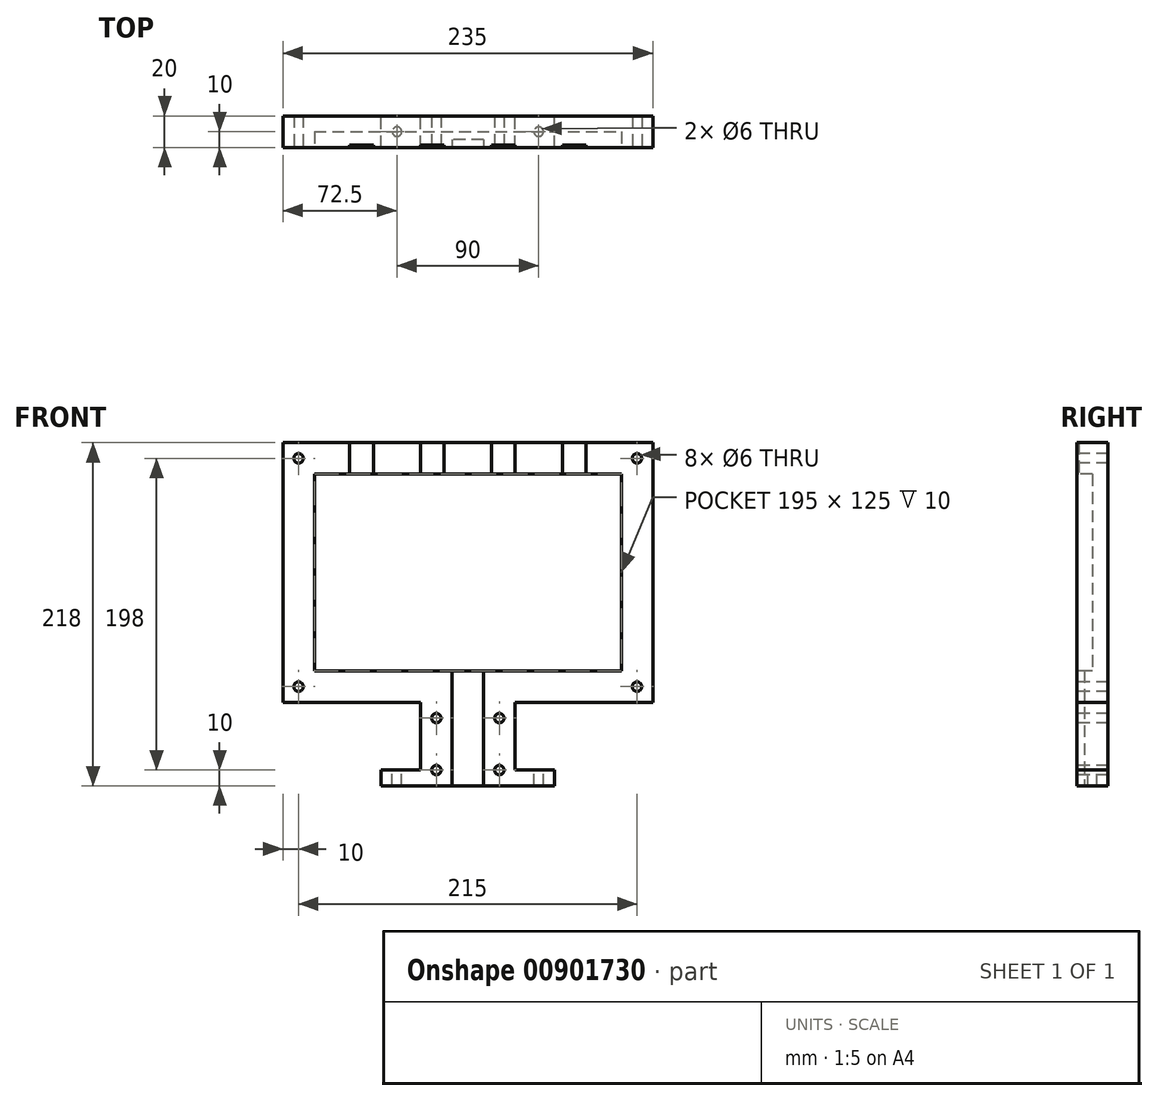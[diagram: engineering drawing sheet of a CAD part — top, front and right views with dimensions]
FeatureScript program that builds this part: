
annotation { "Feature Type Name" : "Feature", "Feature Type Description" : "" }
export const myFeature = defineFeature(function(context is Context, id is Id, definition is map)
    precondition{}
    {
        {
            var Q0;
            Q0=qCreatedBy(makeId("Front.planeOp"),FACE);
            var sketch = newSketch(context, id + "F0", { "sketchPlane" : qUnion([Q0])});
            skLineSegment(sketch, "E0", {"start": v(0, 0) * mm, "end": v(0, 10) * mm});
            skLineSegment(sketch, "E1", {"start": v(0, 10) * mm, "end": v(25, 10) * mm});
            skLineSegment(sketch, "E2", {"start": v(25, 10) * mm, "end": v(25, 53) * mm});
            skLineSegment(sketch, "E3", {"start": v(25, 53) * mm, "end": v(-62.5, 53) * mm});
            skLineSegment(sketch, "E4", {"start": v(-62.5, 53) * mm, "end": v(-62.5, 218) * mm});
            skLineSegment(sketch, "E5", {"start": v(-62.5, 218) * mm, "end": v(172.5, 218) * mm});
            skLineSegment(sketch, "E6", {"start": v(172.5, 218) * mm, "end": v(172.5, 53) * mm});
            skLineSegment(sketch, "E7", {"start": v(172.5, 53) * mm, "end": v(85, 53) * mm});
            skLineSegment(sketch, "E8", {"start": v(85, 53) * mm, "end": v(85, 10) * mm});
            skLineSegment(sketch, "E9", {"start": v(85, 10) * mm, "end": v(110, 10) * mm});
            skLineSegment(sketch, "E10", {"start": v(110, 10) * mm, "end": v(110, 0) * mm});
            skLineSegment(sketch, "E11", {"start": v(110, 0) * mm, "end": v(0, 0) * mm});
            skSolve(sketch);
        }
        {
            var Q0;
            Q0=makeQuery(id+"F0.imprint","IMPRINT",FACE,{"disambiguationData":[TD([[makeQuery(id+"F0.imprint","IMPRINT",EDGE,{"derivedFrom":sQuery(id+"F0.wireOp",EDGE,"E0")}),-1.0]])]});
            extrude(context, id + "F1", {"entities" : qUnion([Q0]), "depth" : 20 * mm, "offsetDistance" : 25 * mm});
        }
        {
            var Q0;
            Q0=makeQuery(id+"F1.opExtrude","CAP_FACE",FACE,{"disambiguationData":[OSD([sQuery(id+"F0.wireOp",EDGE,"E0"),sQuery(id+"F0.wireOp",EDGE,"E1"),sQuery(id+"F0.wireOp",EDGE,"E2"),sQuery(id+"F0.wireOp",EDGE,"E3"),sQuery(id+"F0.wireOp",EDGE,"E4"),sQuery(id+"F0.wireOp",EDGE,"E5"),sQuery(id+"F0.wireOp",EDGE,"E6"),sQuery(id+"F0.wireOp",EDGE,"E7"),sQuery(id+"F0.wireOp",EDGE,"E8"),sQuery(id+"F0.wireOp",EDGE,"E9"),sQuery(id+"F0.wireOp",EDGE,"E10"),sQuery(id+"F0.wireOp",EDGE,"E11")])],"isStart":false});
            var sketch = newSketch(context, id + "F2", { "sketchPlane" : qUnion([Q0])});
            skSolve(sketch);
        }
        {
            var Q0;
            Q0=makeQuery(id+"F2.imprint","IMPRINT",FACE,{"disambiguationData":[TD([[makeQuery(id+"F2.imprint","IMPRINT",EDGE,{"derivedFrom":makeQuery(id+"F1.opExtrude","CAP_EDGE",EDGE,{"disambiguationData":[OSD([sQuery(id+"F0.wireOp",EDGE,"E0")])],"isStart":false})}),-1.0]])]});
            var sketch = newSketch(context, id + "F3", { "sketchPlane" : qUnion([Q0])});
            skLineSegment(sketch, "E12.bottom", {"start": v(-42.5, 198) * mm, "end": v(152.5, 198) * mm});
            skLineSegment(sketch, "E12.top", {"start": v(-42.5, 73) * mm, "end": v(152.5, 73) * mm});
            skLineSegment(sketch, "E12.left", {"start": v(-42.5, 198) * mm, "end": v(-42.5, 73) * mm});
            skLineSegment(sketch, "E12.right", {"start": v(152.5, 198) * mm, "end": v(152.5, 73) * mm});
            skSolve(sketch);
        }
        {
            var Q0;
            Q0 = qSketchRegion(id + "F3", true);
            extrude(context, id + "F4", {"entities" : qUnion([Q0]), "operationType" : NewBodyOperationType.REMOVE, "oppositeDirection" : true, "depth" : 10 * mm, "offsetDistance" : 25 * mm});
        }
        {
            var Q0;
            Q0=makeQuery(id+"F2.imprint","IMPRINT",FACE,{"disambiguationData":[TD([[makeQuery(id+"F2.imprint","IMPRINT",EDGE,{"derivedFrom":makeQuery(id+"F1.opExtrude","CAP_EDGE",EDGE,{"disambiguationData":[OSD([sQuery(id+"F0.wireOp",EDGE,"E0")])],"isStart":false})}),-1.0]])]});
            var sketch = newSketch(context, id + "F5", { "sketchPlane" : qUnion([Q0])});
            skLineSegment(sketch, "E13.bottom", {"start": v(45, 73) * mm, "end": v(65, 73) * mm});
            skLineSegment(sketch, "E13.top", {"start": v(45, 0) * mm, "end": v(65, 0) * mm});
            skLineSegment(sketch, "E13.left", {"start": v(45, 73) * mm, "end": v(45, 0) * mm});
            skLineSegment(sketch, "E13.right", {"start": v(65, 73) * mm, "end": v(65, 0) * mm});
            skSolve(sketch);
        }
        {
            var Q0;
            Q0 = qSketchRegion(id + "F5", true);
            extrude(context, id + "F6", {"entities" : qUnion([Q0]), "operationType" : NewBodyOperationType.REMOVE, "oppositeDirection" : true, "depth" : 5 * mm, "offsetDistance" : 25 * mm});
        }
        {
            var Q0;
            Q0=makeQuery(id+"F2.imprint","IMPRINT",FACE,{"disambiguationData":[TD([[makeQuery(id+"F2.imprint","IMPRINT",EDGE,{"derivedFrom":makeQuery(id+"F1.opExtrude","CAP_EDGE",EDGE,{"disambiguationData":[OSD([sQuery(id+"F0.wireOp",EDGE,"E0")])],"isStart":false})}),-1.0]])]});
            var sketch = newSketch(context, id + "F7", { "sketchPlane" : qUnion([Q0])});
            skCircle(sketch, "E14", {"center": v(-52.5, 208) * mm, "radius": 3 * mm});
            skCircle(sketch, "E15", {"center": v(162.5, 208) * mm, "radius": 3 * mm});
            skCircle(sketch, "E16", {"center": v(162.5, 63) * mm, "radius": 3 * mm});
            skCircle(sketch, "E17", {"center": v(-52.5, 63) * mm, "radius": 3 * mm});
            skCircle(sketch, "E18", {"center": v(35, 10) * mm, "radius": 3 * mm});
            skCircle(sketch, "E19", {"center": v(35, 43) * mm, "radius": 3 * mm});
            skCircle(sketch, "E20", {"center": v(75, 43) * mm, "radius": 3 * mm});
            skCircle(sketch, "E21", {"center": v(75, 10) * mm, "radius": 3 * mm});
            skSolve(sketch);
        }
        {
            var Q0;
            Q0 = qSketchRegion(id + "F7", true);
            extrude(context, id + "F8", {"entities" : qUnion([Q0]), "operationType" : NewBodyOperationType.REMOVE, "endBound" : BoundingType.THROUGH_ALL, "oppositeDirection" : true, "depth" : 25 * mm, "offsetDistance" : 25 * mm});
        }
        {
            var Q0;
            Q0=makeQuery(id+"F1.opExtrude","SWEPT_FACE",FACE,{"disambiguationData":[OSD([sQuery(id+"F0.wireOp",EDGE,"E1")])]});
            var sketch = newSketch(context, id + "F9", { "sketchPlane" : qUnion([Q0])});
            skCircle(sketch, "E22", {"center": v(10, -10) * mm, "radius": 3 * mm});
            skCircle(sketch, "E23", {"center": v(100, -10) * mm, "radius": 3 * mm});
            skSolve(sketch);
        }
        {
            var Q0;
            Q0 = qSketchRegion(id + "F9", true);
            extrude(context, id + "F10", {"entities" : qUnion([Q0]), "operationType" : NewBodyOperationType.REMOVE, "endBound" : BoundingType.THROUGH_ALL, "oppositeDirection" : true, "depth" : 25 * mm, "offsetDistance" : 25 * mm});
        }
        {
            var Q0;
            Q0=makeQuery(id+"F2.imprint","IMPRINT",FACE,{"disambiguationData":[TD([[makeQuery(id+"F2.imprint","IMPRINT",EDGE,{"derivedFrom":makeQuery(id+"F1.opExtrude","CAP_EDGE",EDGE,{"disambiguationData":[OSD([sQuery(id+"F0.wireOp",EDGE,"E0")])],"isStart":false})}),-1.0]])]});
            var sketch = newSketch(context, id + "F11", { "sketchPlane" : qUnion([Q0])});
            skSolve(sketch);
        }
        {
            var Q0;
            Q0=makeQuery(id+"F11.imprint","IMPRINT",FACE,{"disambiguationData":[TD([[makeQuery(id+"F11.imprint","IMPRINT",EDGE,{"derivedFrom":makeQuery(id+"F2.imprint","IMPRINT",EDGE,{"derivedFrom":makeQuery(id+"F1.opExtrude","CAP_EDGE",EDGE,{"disambiguationData":[OSD([sQuery(id+"F0.wireOp",EDGE,"E0")])],"isStart":false})})}),-1.0]])]});
            var sketch = newSketch(context, id + "F12", { "sketchPlane" : qUnion([Q0])});
            skLineSegment(sketch, "E24.bottom", {"start": v(-20, 218) * mm, "end": v(-5, 218) * mm});
            skLineSegment(sketch, "E24.top", {"start": v(-20, 198) * mm, "end": v(-5, 198) * mm});
            skLineSegment(sketch, "E24.left", {"start": v(-20, 218) * mm, "end": v(-20, 198) * mm});
            skLineSegment(sketch, "E24.right", {"start": v(-5, 218) * mm, "end": v(-5, 198) * mm});
            skLineSegment(sketch, "E25.bottom", {"start": v(25, 218) * mm, "end": v(40, 218) * mm});
            skLineSegment(sketch, "E25.top", {"start": v(25, 198) * mm, "end": v(40, 198) * mm});
            skLineSegment(sketch, "E25.left", {"start": v(25, 218) * mm, "end": v(25, 198) * mm});
            skLineSegment(sketch, "E25.right", {"start": v(40, 218) * mm, "end": v(40, 198) * mm});
            skLineSegment(sketch, "E26.bottom", {"start": v(70, 218) * mm, "end": v(85, 218) * mm});
            skLineSegment(sketch, "E26.top", {"start": v(70, 198) * mm, "end": v(85, 198) * mm});
            skLineSegment(sketch, "E26.left", {"start": v(70, 218) * mm, "end": v(70, 198) * mm});
            skLineSegment(sketch, "E26.right", {"start": v(85, 218) * mm, "end": v(85, 198) * mm});
            skLineSegment(sketch, "E27.bottom", {"start": v(115, 218) * mm, "end": v(130, 218) * mm});
            skLineSegment(sketch, "E27.top", {"start": v(115, 198) * mm, "end": v(130, 198) * mm});
            skLineSegment(sketch, "E27.left", {"start": v(115, 218) * mm, "end": v(115, 198) * mm});
            skLineSegment(sketch, "E27.right", {"start": v(130, 218) * mm, "end": v(130, 198) * mm});
            skSolve(sketch);
        }
        {
            var Q0;
            Q0 = qSketchRegion(id + "F12", true);
            extrude(context, id + "F13", {"entities" : qUnion([Q0]), "operationType" : NewBodyOperationType.REMOVE, "oppositeDirection" : true, "depth" : 1.5 * mm, "offsetDistance" : 25 * mm});
        }
    });
